# Revit family: 1394003, 1394004 - Mitsu Wall (RFA)-
name_source: partatom
category: Lighting Fixtures
revit_build: Autodesk Revit 2018 (Build: 20170223_1515(x64)
units: mm (PartAtom-declared; Revit-internal decimal feet)

## family parameters
Always vertical = Yes
Cut with Voids When Loaded = No
Host = Wall
Light Source = No
OmniClass Number = 23.80.70.00
OmniClass Title = Lighting
Part Type = Normal
Room Calculation Point = No
Round Connector Dimension = Use Diameter
Shared = No

## types (2) — shared parameters
Driver Required = No
Main Material = Metal - Steel
Manufacturer = Astro Lighting Ltd
Manufacturer URL - Europe and Rest of World = www.astrolighting.com
Manufacturer URL - North America = us.astrolighting.com
Product CCT = 2700K / 3000K
Product CRI = 80 / 90
URL = www.astrolighting.com

## per-type parameters (varying)
| type | ADA compliant | Dimmable | Dimming Method | Driver Included | Efficacy (lm/w) | Electrical Class | Lamp | Length of Cable Supplied | Light Source Fixed | Location / IP Rating | Main Finish | Power (Watts) | Product Dimensions (MM) | Product Location | Product Name | Product SKU | Product Weight (KG) |
| CE | N / A | No | Lamp Dependent | Not Applicable | Lamp Dependent | 1 | LED | Not Applicable | Yes | IP20 | Various | Lamp Dependent | 235 x 173 x 208 | Indoor | Mitsu Wall | 1394004 | 0.7 |
| ETL |  |  |  |  |  | 0 |  |  |  | DAMP |  |  |  | Bathroom |  | 1234001 |  |

## geometry (parser evidence)
native form markers: Sweep x2
no freeform markers — native parametric forms only
